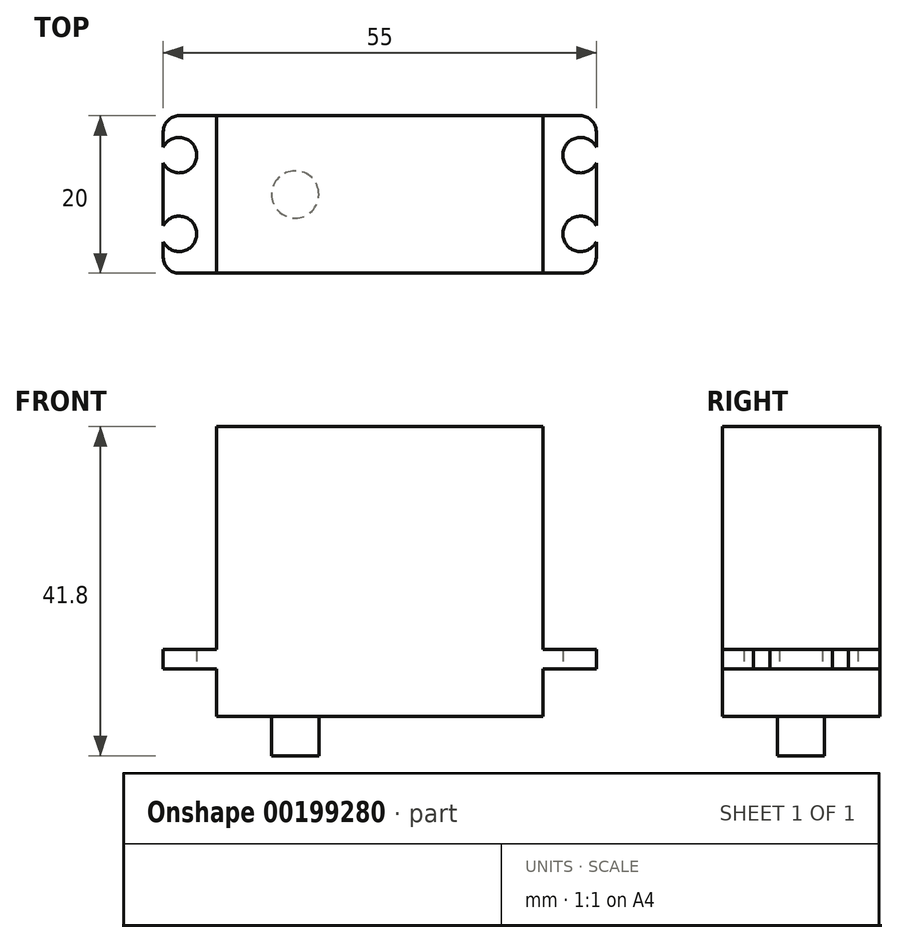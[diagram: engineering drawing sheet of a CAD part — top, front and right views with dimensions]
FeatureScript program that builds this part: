
annotation { "Feature Type Name" : "Feature", "Feature Type Description" : "" }
export const myFeature = defineFeature(function(context is Context, id is Id, definition is map)
    precondition{}
    {
        {
            var Q0;
            Q0=qCreatedBy(makeId("Front.planeOp"),FACE);
            var sketch = newSketch(context, id + "F0", { "sketchPlane" : qUnion([Q0])});
            skLineSegment(sketch, "E0.bottom", {"start": v(-20.75, 18.4) * mm, "end": v(20.75, 18.4) * mm});
            skLineSegment(sketch, "E0.top", {"start": v(-20.75, -18.4) * mm, "end": v(20.75, -18.4) * mm});
            skLineSegment(sketch, "E0.left", {"start": v(-20.75, 18.4) * mm, "end": v(-20.75, -18.4) * mm});
            skLineSegment(sketch, "E0.right", {"start": v(20.75, 18.4) * mm, "end": v(20.75, -18.4) * mm});
            skPoint(sketch, "E0.middle", {"position": v(0, 0) * mm});
            skSolve(sketch);
        }
        {
            var Q0;
            Q0 = qSketchRegion(id + "F0", true);
            extrude(context, id + "F1", {"entities" : qUnion([Q0]), "depth" : 20 * mm});
        }
        {
            var Q0;
            Q0=makeQuery(id+"F1.opExtrude","CAP_FACE",FACE,{"disambiguationData":[OSD([sQuery(id+"F0.wireOp",EDGE,"E0.bottom"),sQuery(id+"F0.wireOp",EDGE,"E0.top"),sQuery(id+"F0.wireOp",EDGE,"E0.left"),sQuery(id+"F0.wireOp",EDGE,"E0.right")])],"isStart":false});
            var sketch = newSketch(context, id + "F2", { "sketchPlane" : qUnion([Q0])});
            skLineSegment(sketch, "E1.bottom", {"start": v(-27.5, -9.9) * mm, "end": v(27.5, -9.9) * mm});
            skLineSegment(sketch, "E1.top", {"start": v(-27.5, -12.4) * mm, "end": v(27.5, -12.4) * mm});
            skLineSegment(sketch, "E1.left", {"start": v(-27.5, -9.9) * mm, "end": v(-27.5, -12.4) * mm});
            skLineSegment(sketch, "E1.right", {"start": v(27.5, -9.9) * mm, "end": v(27.5, -12.4) * mm});
            skPoint(sketch, "E1.middle", {"position": v(0, -11.15) * mm});
            skSolve(sketch);
        }
        {
            var Q0;
            Q0 = qSketchRegion(id + "F2", true);
            extrude(context, id + "F3", {"entities" : qUnion([Q0]), "operationType" : NewBodyOperationType.ADD, "oppositeDirection" : true, "depth" : 20 * mm});
        }
        {
            var Q0;
            Q0=makeQuery(id+"F1.opExtrude","SWEPT_FACE",FACE,{"disambiguationData":[OSD([sQuery(id+"F0.wireOp",EDGE,"E0.top")])]});
            var sketch = newSketch(context, id + "F4", { "sketchPlane" : qUnion([Q0])});
            skCircle(sketch, "E2", {"center": v(-10.75, 10) * mm, "radius": 3 * mm});
            skPoint(sketch, "E2.centerSnap0", {"position": v(-20.75, 10) * mm});
            skSolve(sketch);
        }
        {
            var Q0;
            Q0 = qSketchRegion(id + "F4", true);
            extrude(context, id + "F5", {"entities" : qUnion([Q0]), "operationType" : NewBodyOperationType.ADD, "depth" : 5 * mm});
        }
        {
            var Q0;
            {var subQ0=sQuery(id+"F0.wireOp",EDGE,"E0.right");var subQ6=sQuery(id+"F2.wireOp",EDGE,"E1.top");Q0=makeQuery(id+"F3.boolean.opBoolean","SPLIT",FACE,{"disambiguationData":[TD([makeQuery(id+"F1.opExtrude","SWEPT_FACE",FACE,{"disambiguationData":[OSD([subQ0])]})])],"derivedFrom":makeQuery(id+"F3.opExtrude","SWEPT_FACE",FACE,{"disambiguationData":[OSD([subQ6])]})});}
            var sketch = newSketch(context, id + "F6", { "sketchPlane" : qUnion([Q0])});
            skLineSegment(sketch, "E3", {"start": v(27.5, 10) * mm, "end": v(-27.41, 10) * mm, "construction": true});
            skCircle(sketch, "E4", {"center": v(-25.5, 15) * mm, "radius": 2.25 * mm});
            skCircle(sketch, "E5.MirrorC", {"center": v(-25.5, 5) * mm, "radius": 2.25 * mm});
            skLineSegment(sketch, "E6", {"start": v(0, 20.18) * mm, "end": v(0, 0) * mm, "construction": true});
            skCircle(sketch, "E7.MirrorC", {"center": v(25.5, 15) * mm, "radius": 2.25 * mm});
            skCircle(sketch, "E8.MirrorC", {"center": v(25.5, 5) * mm, "radius": 2.25 * mm});
            skSolve(sketch);
        }
        {
            var Q0;
            Q0 = qSketchRegion(id + "F6", true);
            extrude(context, id + "F7", {"entities" : qUnion([Q0]), "operationType" : NewBodyOperationType.REMOVE, "oppositeDirection" : true, "depth" : 25 * mm});
        }
        {
            var Q0;
            Q0=makeQuery(id+"F3.opExtrude","CAP_EDGE",EDGE,{"disambiguationData":[OSD([sQuery(id+"F2.wireOp",EDGE,"E1.right")])],"isStart":true});
            var Q1;
            Q1=makeQuery(id+"F3.opExtrude","CAP_EDGE",EDGE,{"disambiguationData":[OSD([sQuery(id+"F2.wireOp",EDGE,"E1.right")])],"isStart":false});
            var Q2;
            Q2=makeQuery(id+"F3.opExtrude","CAP_EDGE",EDGE,{"disambiguationData":[OSD([sQuery(id+"F2.wireOp",EDGE,"E1.left")])],"isStart":true});
            var Q3;
            Q3=makeQuery(id+"F3.opExtrude","CAP_EDGE",EDGE,{"disambiguationData":[OSD([sQuery(id+"F2.wireOp",EDGE,"E1.left")])],"isStart":false});
            fillet(context, id + "F8", {"entities" : qUnion([Q0, Q1, Q2, Q3]), "radius" : 2 * mm, "tangentPropagation" : true, "allowEdgeOverflow" : false});
        }
    });
